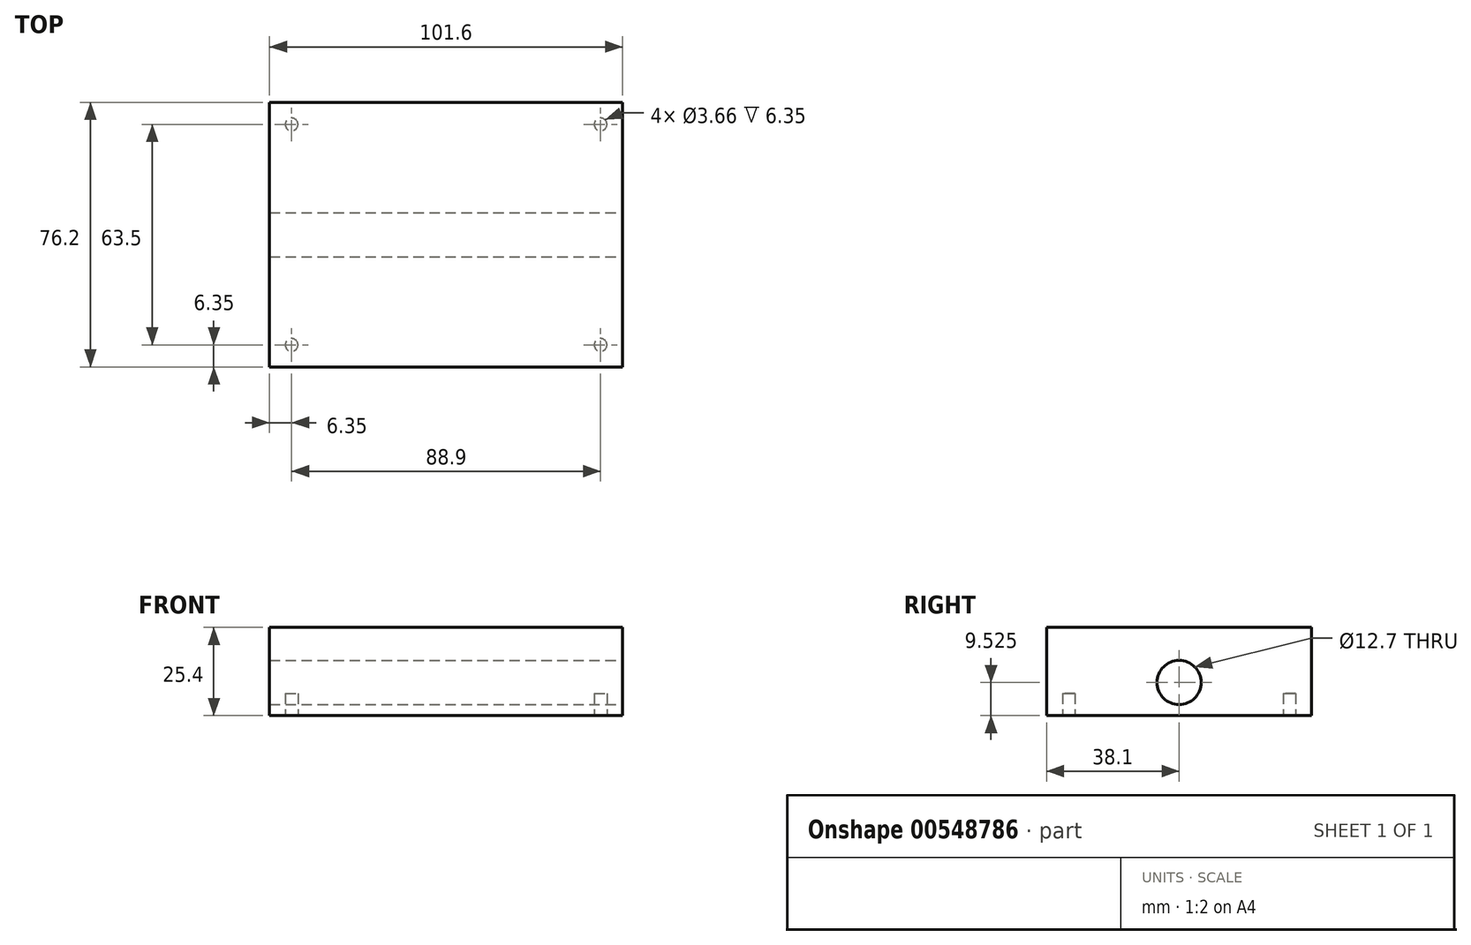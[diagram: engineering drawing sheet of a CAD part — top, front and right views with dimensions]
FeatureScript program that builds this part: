
annotation { "Feature Type Name" : "Feature", "Feature Type Description" : "" }
export const myFeature = defineFeature(function(context is Context, id is Id, definition is map)
    precondition{}
    {
        {
            var Q0;
            Q0=qCreatedBy(makeId("Top.planeOp"),FACE);
            var sketch = newSketch(context, id + "F0", { "sketchPlane" : qUnion([Q0])});
            skLineSegment(sketch, "E0.bottom", {"start": v(-50.8, 38.1) * mm, "end": v(50.8, 38.1) * mm});
            skLineSegment(sketch, "E0.top", {"start": v(-50.8, -38.1) * mm, "end": v(50.8, -38.1) * mm});
            skLineSegment(sketch, "E0.left", {"start": v(-50.8, 38.1) * mm, "end": v(-50.8, -38.1) * mm});
            skLineSegment(sketch, "E0.right", {"start": v(50.8, 38.1) * mm, "end": v(50.8, -38.1) * mm});
            skLineSegment(sketch, "E1", {"start": v(0, 0) * mm, "end": v(0, 38.1) * mm, "construction": true});
            skLineSegment(sketch, "E2", {"start": v(0, 0) * mm, "end": v(50.8, 0) * mm, "construction": true});
            skSolve(sketch);
        }
        {
            var Q0;
            Q0=makeQuery(id+"F0.imprint","IMPRINT",FACE,{"disambiguationData":[TD([[makeQuery(id+"F0.imprint","IMPRINT",EDGE,{"derivedFrom":sQuery(id+"F0.wireOp",EDGE,"E0.bottom")}),-1.0]])]});
            extrude(context, id + "F1", {"entities" : qUnion([Q0]), "depth" : 25.4 * mm, "offsetDistance" : 25.4 * mm});
        }
        {
            var Q0;
            Q0=makeQuery(id+"F1.opExtrude","SWEPT_FACE",FACE,{"disambiguationData":[OSD([sQuery(id+"F0.wireOp",EDGE,"E0.right")])]});
            var sketch = newSketch(context, id + "F2", { "sketchPlane" : qUnion([Q0])});
            skCircle(sketch, "E3", {"center": v(0, 9.53) * mm, "radius": 6.35 * mm});
            skLineSegment(sketch, "E4", {"start": v(0, 9.53) * mm, "end": v(0, 0) * mm, "construction": true});
            skSolve(sketch);
        }
        {
            var Q0;
            Q0=makeQuery(id+"F2.imprint","IMPRINT",FACE,{"disambiguationData":[TD([[makeQuery(id+"F2.imprint","IMPRINT",EDGE,{"derivedFrom":sQuery(id+"F2.wireOp",EDGE,"E3")}),1.0]])]});
            extrude(context, id + "F3", {"entities" : qUnion([Q0]), "operationType" : NewBodyOperationType.REMOVE, "oppositeDirection" : true, "depth" : 101.6 * mm, "offsetDistance" : 25.4 * mm});
        }
        {
            var Q0;
            Q0=makeQuery(id+"F1.opExtrude","CAP_FACE",FACE,{"disambiguationData":[OSD([sQuery(id+"F0.wireOp",EDGE,"E0.bottom"),sQuery(id+"F0.wireOp",EDGE,"E0.top"),sQuery(id+"F0.wireOp",EDGE,"E0.left"),sQuery(id+"F0.wireOp",EDGE,"E0.right")])],"isStart":true});
            var sketch = newSketch(context, id + "F4", { "sketchPlane" : qUnion([Q0])});
            skLineSegment(sketch, "E5.bottom", {"start": v(-44.45, 31.75) * mm, "end": v(44.45, 31.75) * mm, "construction": true});
            skLineSegment(sketch, "E5.top", {"start": v(-44.45, -31.75) * mm, "end": v(44.45, -31.75) * mm, "construction": true});
            skLineSegment(sketch, "E5.left", {"start": v(-44.45, 31.75) * mm, "end": v(-44.45, -31.75) * mm, "construction": true});
            skLineSegment(sketch, "E5.right", {"start": v(44.45, 31.75) * mm, "end": v(44.45, -31.75) * mm, "construction": true});
            skPoint(sketch, "E5.middle", {"position": v(0, 0) * mm});
            skCircle(sketch, "E6", {"center": v(-44.45, 31.75) * mm, "radius": 1.83 * mm});
            skCircle(sketch, "E7", {"center": v(44.45, 31.75) * mm, "radius": 1.83 * mm});
            skCircle(sketch, "E8", {"center": v(44.45, -31.75) * mm, "radius": 1.83 * mm});
            skCircle(sketch, "E9", {"center": v(-44.45, -31.75) * mm, "radius": 1.83 * mm});
            skSolve(sketch);
        }
        {
            var Q0;
            Q0=makeQuery(id+"F4.imprint","IMPRINT",FACE,{"disambiguationData":[TD([[makeQuery(id+"F4.imprint","IMPRINT",EDGE,{"derivedFrom":sQuery(id+"F4.wireOp",EDGE,"E6")}),1.0]])]});
            var Q1;
            Q1=makeQuery(id+"F4.imprint","IMPRINT",FACE,{"disambiguationData":[TD([[makeQuery(id+"F4.imprint","IMPRINT",EDGE,{"derivedFrom":sQuery(id+"F4.wireOp",EDGE,"E9")}),1.0]])]});
            var Q2;
            Q2=makeQuery(id+"F4.imprint","IMPRINT",FACE,{"disambiguationData":[TD([[makeQuery(id+"F4.imprint","IMPRINT",EDGE,{"derivedFrom":sQuery(id+"F4.wireOp",EDGE,"E8")}),1.0]])]});
            var Q3;
            Q3=makeQuery(id+"F4.imprint","IMPRINT",FACE,{"disambiguationData":[TD([[makeQuery(id+"F4.imprint","IMPRINT",EDGE,{"derivedFrom":sQuery(id+"F4.wireOp",EDGE,"E7")}),1.0]])]});
            extrude(context, id + "F5", {"entities" : qUnion([Q0, Q1, Q2, Q3]), "operationType" : NewBodyOperationType.REMOVE, "oppositeDirection" : true, "depth" : 6.35 * mm, "offsetDistance" : 25.4 * mm});
        }
    });
